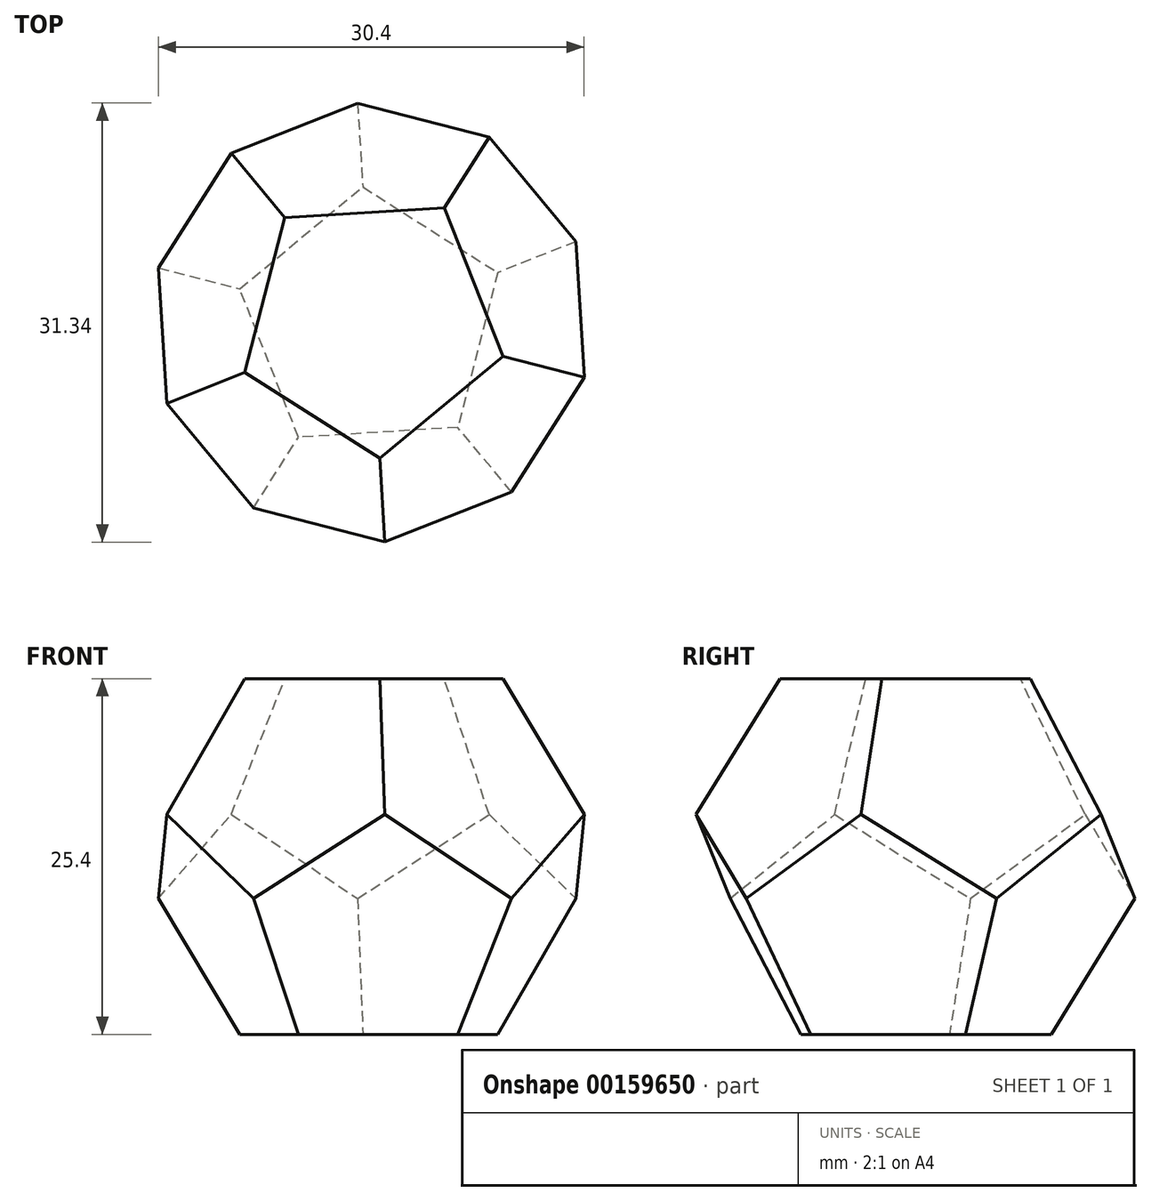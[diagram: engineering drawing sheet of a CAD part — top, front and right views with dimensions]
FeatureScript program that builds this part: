
annotation { "Feature Type Name" : "Feature", "Feature Type Description" : "" }
export const myFeature = defineFeature(function(context is Context, id is Id, definition is map)
    precondition{}
    {
        {
            assignVariable(context, id + "F0", {"name" : "height", "anyValue" : 25.4 * mm});
        }
        {
            var Q0;
            Q0=qCreatedBy(makeId("Top.planeOp"),FACE);
            var sketch = newSketch(context, id + "F1", { "sketchPlane" : qUnion([Q0])});
            skCircle(sketch, "E0.cCircle", {"center": v(0, 0) * mm, "radius": 7.85 * mm, "construction": true});
            skLineSegment(sketch, "E0.0", {"start": v(-0.6, 9.68) * mm, "end": v(9.02, 3.57) * mm});
            skLineSegment(sketch, "E0.1", {"start": v(9.02, 3.57) * mm, "end": v(6.18, -7.48) * mm});
            skLineSegment(sketch, "E0.2", {"start": v(6.18, -7.48) * mm, "end": v(-5.2, -8.19) * mm});
            skLineSegment(sketch, "E0.3", {"start": v(-5.2, -8.19) * mm, "end": v(-9.4, 2.42) * mm});
            skLineSegment(sketch, "E0.4", {"start": v(-9.4, 2.42) * mm, "end": v(-0.6, 9.68) * mm});
            skPoint(sketch, "E0.0.midPoint", {"position": v(4.2, 6.62) * mm});
            skCircle(sketch, "E1", {"center": v(0, 0) * mm, "radius": 9.7 * mm});
            skSolve(sketch);
        }
        {
            var Q0;
            Q0=makeQuery(id+"F1.imprint","IMPRINT",FACE,{"disambiguationData":[TD([[makeQuery(id+"F1.imprint","IMPRINT",EDGE,{"derivedFrom":sQuery(id+"F1.wireOp",EDGE,"E0.0")}),-1.0]])]});
            extrude(context, id + "F2", {"entities" : qUnion([Q0]), "depth" : getVariable(context, 'height'), "hasDraft" : true, "draftAngle" : 26.57 * degree});
        }
        {
            var Q0;
            Q0=makeQuery(id+"F2.opExtrude","CAP_FACE",FACE,{"disambiguationData":[OSD([sQuery(id+"F1.wireOp",EDGE,"E0.0"),sQuery(id+"F1.wireOp",EDGE,"E0.1"),sQuery(id+"F1.wireOp",EDGE,"E0.2"),sQuery(id+"F1.wireOp",EDGE,"E0.3"),sQuery(id+"F1.wireOp",EDGE,"E0.4")])],"isStart":false});
            var sketch = newSketch(context, id + "F3", { "sketchPlane" : qUnion([Q0])});
            skPoint(sketch, "E2.0.end.orphan", {"position": v(-9.4, 2.42) * mm});
            skPoint(sketch, "E2.0.start.orphan", {"position": v(-5.2, -8.19) * mm});
            skPoint(sketch, "E3.0.end.orphan", {"position": v(6.18, -7.48) * mm});
            skPoint(sketch, "E4.0.end.orphan", {"position": v(9.02, 3.57) * mm});
            skPoint(sketch, "E4.0.start.orphan", {"position": v(-0.6, 9.68) * mm});
            skCircle(sketch, "E5.cCircle", {"center": v(0, 0) * mm, "radius": 9.7 * mm, "construction": true});
            skLineSegment(sketch, "E5.0", {"start": v(0.6, -9.68) * mm, "end": v(-9.02, -3.57) * mm});
            skLineSegment(sketch, "E5.1", {"start": v(-9.02, -3.57) * mm, "end": v(-6.18, 7.48) * mm});
            skLineSegment(sketch, "E5.2", {"start": v(-6.18, 7.48) * mm, "end": v(5.2, 8.19) * mm});
            skLineSegment(sketch, "E5.3", {"start": v(5.2, 8.19) * mm, "end": v(9.4, -2.42) * mm});
            skLineSegment(sketch, "E5.4", {"start": v(9.4, -2.42) * mm, "end": v(0.6, -9.68) * mm});
            skLineSegment(sketch, "E6", {"start": v(-1.58, 25.35) * mm, "end": v(-0.49, 7.83) * mm});
            skSolve(sketch);
        }
        {
            var Q0;
            Q0=makeQuery(id+"F3.imprint","IMPRINT",FACE,{"disambiguationData":[TD([[makeQuery(id+"F3.imprint","IMPRINT",EDGE,{"derivedFrom":sQuery(id+"F3.wireOp",EDGE,"E5.0")}),-1.0]])]});
            extrude(context, id + "F4", {"entities" : qUnion([Q0]), "oppositeDirection" : true, "depth" : getVariable(context, 'height'), "hasDraft" : true, "draftAngle" : 26.57 * degree});
        }
        {
            var Q0;
            Q0=makeQuery(id+"F2.opExtrude","SWEPT_BODY",BODY,{"disambiguationData":[OSD([sQuery(id+"F1.wireOp",EDGE,"E0.0"),sQuery(id+"F1.wireOp",EDGE,"E0.1"),sQuery(id+"F1.wireOp",EDGE,"E0.2"),sQuery(id+"F1.wireOp",EDGE,"E0.3"),sQuery(id+"F1.wireOp",EDGE,"E0.4")])]});
            var Q1;
            Q1=makeQuery(id+"F4.opExtrude","SWEPT_BODY",BODY,{"disambiguationData":[OSD([sQuery(id+"F3.wireOp",EDGE,"E5.0"),sQuery(id+"F3.wireOp",EDGE,"E5.1"),sQuery(id+"F3.wireOp",EDGE,"E5.2"),sQuery(id+"F3.wireOp",EDGE,"E5.3"),sQuery(id+"F3.wireOp",EDGE,"E5.4")])]});
            booleanBodies(context, id + "F5", {"operationType" : BooleanOperationType.INTERSECTION, "tools" : qUnion([Q0, Q1])});
        }
    });
